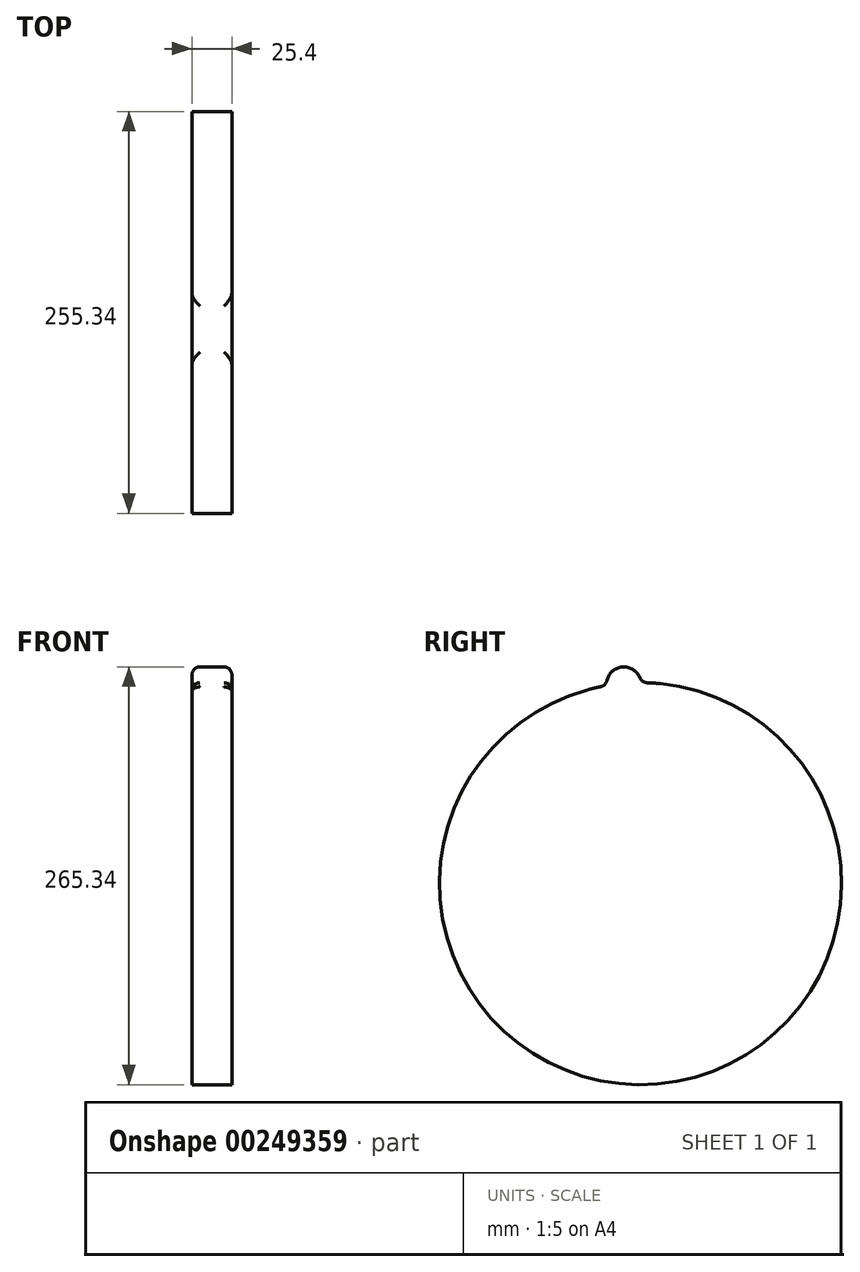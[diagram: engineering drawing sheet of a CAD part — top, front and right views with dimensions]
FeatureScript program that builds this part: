
annotation { "Feature Type Name" : "Feature", "Feature Type Description" : "" }
export const myFeature = defineFeature(function(context is Context, id is Id, definition is map)
    precondition{}
    {
        {
            var Q0;
            Q0=qCreatedBy(makeId("Right.planeOp"),FACE);
            var sketch = newSketch(context, id + "F0", { "sketchPlane" : qUnion([Q0])});
            skCircle(sketch, "E0", {"center": v(0, 0) * mm, "radius": 127.67 * mm});
            skSolve(sketch);
        }
        {
            var Q0;
            Q0=makeQuery(id+"F0.imprint","IMPRINT",FACE,{"disambiguationData":[TD([[makeQuery(id+"F0.imprint","IMPRINT",EDGE,{"derivedFrom":sQuery(id+"F0.wireOp",EDGE,"E0")}),1.0]])]});
            var sketch = newSketch(context, id + "F1", { "sketchPlane" : qUnion([Q0])});
            skCircle(sketch, "E1", {"center": v(-10.62, 126.68) * mm, "radius": 11 * mm});
            skSolve(sketch);
        }
        {
            var Q0;
            Q0=makeQuery(id+"FbJOAYsaVXvaVcf_0.36.F1.imprint","IMPRINT",FACE,{"disambiguationData":[TD([[makeQuery(id+"FbJOAYsaVXvaVcf_0.36.F1.imprint","IMPRINT",EDGE,{"derivedFrom":sQuery(id+"FbJOAYsaVXvaVcf_0.36.F1.wireOp",EDGE,"E1")}),1.0]])]});
            var Q1;
            Q1=makeQuery(id+"FbJOAYsaVXvaVcf_0.32.F1.imprint","IMPRINT",FACE,{"disambiguationData":[TD([[makeQuery(id+"FbJOAYsaVXvaVcf_0.32.F1.imprint","IMPRINT",EDGE,{"derivedFrom":sQuery(id+"FbJOAYsaVXvaVcf_0.32.F1.wireOp",EDGE,"E1")}),1.0]])]});
            var Q2;
            Q2=makeQuery(id+"FbJOAYsaVXvaVcf_0.42.F1.imprint","IMPRINT",FACE,{"disambiguationData":[TD([[makeQuery(id+"FbJOAYsaVXvaVcf_0.42.F1.imprint","IMPRINT",EDGE,{"derivedFrom":sQuery(id+"FbJOAYsaVXvaVcf_0.42.F1.wireOp",EDGE,"E1")}),1.0]])]});
            var Q3;
            Q3=makeQuery(id+"FbJOAYsaVXvaVcf_0.37.F1.imprint","IMPRINT",FACE,{"disambiguationData":[TD([[makeQuery(id+"FbJOAYsaVXvaVcf_0.37.F1.imprint","IMPRINT",EDGE,{"derivedFrom":sQuery(id+"FbJOAYsaVXvaVcf_0.37.F1.wireOp",EDGE,"E1")}),1.0]])]});
            var Q4;
            {var subQ0=sQuery(id+"F1.wireOp",EDGE,"E1");var subQ1=makeQuery(id+"F0.imprint","IMPRINT",EDGE,{"derivedFrom":sQuery(id+"F0.wireOp",EDGE,"E0")});var subQ2=makeQuery(id+"F1.imprint","INTERSECT",VERTEX,{"disambiguationData":[OD(0.0)],"derivedFrom":[subQ1,subQ0]});Q4=makeQuery(id+"F1.imprint","IMPRINT",FACE,{"disambiguationData":[TD([[makeQuery(id+"F1.imprint","IMPRINT",EDGE,{"disambiguationData":[TD([[subQ2,-1.0]])],"derivedFrom":subQ0}),1.0]])]});}
            var Q5;
            Q5=makeQuery(id+"FbJOAYsaVXvaVcf_0.4.F1.imprint","IMPRINT",FACE,{"disambiguationData":[TD([[makeQuery(id+"FbJOAYsaVXvaVcf_0.4.F1.imprint","IMPRINT",EDGE,{"derivedFrom":sQuery(id+"FbJOAYsaVXvaVcf_0.4.F1.wireOp",EDGE,"E1")}),1.0]])]});
            var Q6;
            Q6=makeQuery(id+"FbJOAYsaVXvaVcf_0.22.F1.imprint","IMPRINT",FACE,{"disambiguationData":[TD([[makeQuery(id+"FbJOAYsaVXvaVcf_0.22.F1.imprint","IMPRINT",EDGE,{"derivedFrom":sQuery(id+"FbJOAYsaVXvaVcf_0.22.F1.wireOp",EDGE,"E1")}),1.0]])]});
            var Q7;
            Q7=makeQuery(id+"FbJOAYsaVXvaVcf_0.9.F1.imprint","IMPRINT",FACE,{"disambiguationData":[TD([[makeQuery(id+"FbJOAYsaVXvaVcf_0.9.F1.imprint","IMPRINT",EDGE,{"derivedFrom":sQuery(id+"FbJOAYsaVXvaVcf_0.9.F1.wireOp",EDGE,"E1")}),1.0]])]});
            var Q8;
            Q8=makeQuery(id+"FbJOAYsaVXvaVcf_0.38.F1.imprint","IMPRINT",FACE,{"disambiguationData":[TD([[makeQuery(id+"FbJOAYsaVXvaVcf_0.38.F1.imprint","IMPRINT",EDGE,{"derivedFrom":sQuery(id+"FbJOAYsaVXvaVcf_0.38.F1.wireOp",EDGE,"E1")}),1.0]])]});
            var Q9;
            Q9=makeQuery(id+"FbJOAYsaVXvaVcf_0.3.F1.imprint","IMPRINT",FACE,{"disambiguationData":[TD([[makeQuery(id+"FbJOAYsaVXvaVcf_0.3.F1.imprint","IMPRINT",EDGE,{"derivedFrom":sQuery(id+"FbJOAYsaVXvaVcf_0.3.F1.wireOp",EDGE,"E1")}),1.0]])]});
            var Q10;
            Q10=makeQuery(id+"FbJOAYsaVXvaVcf_0.34.F1.imprint","IMPRINT",FACE,{"disambiguationData":[TD([[makeQuery(id+"FbJOAYsaVXvaVcf_0.34.F1.imprint","IMPRINT",EDGE,{"derivedFrom":sQuery(id+"FbJOAYsaVXvaVcf_0.34.F1.wireOp",EDGE,"E1")}),1.0]])]});
            var Q11;
            Q11=makeQuery(id+"FbJOAYsaVXvaVcf_0.30.F1.imprint","IMPRINT",FACE,{"disambiguationData":[TD([[makeQuery(id+"FbJOAYsaVXvaVcf_0.30.F1.imprint","IMPRINT",EDGE,{"derivedFrom":sQuery(id+"FbJOAYsaVXvaVcf_0.30.F1.wireOp",EDGE,"E1")}),1.0]])]});
            var Q12;
            Q12=makeQuery(id+"FbJOAYsaVXvaVcf_0.48.F1.imprint","IMPRINT",FACE,{"disambiguationData":[TD([[makeQuery(id+"FbJOAYsaVXvaVcf_0.48.F1.imprint","IMPRINT",EDGE,{"derivedFrom":sQuery(id+"FbJOAYsaVXvaVcf_0.48.F1.wireOp",EDGE,"E1")}),1.0]])]});
            var Q13;
            Q13=makeQuery(id+"FbJOAYsaVXvaVcf_0.44.F1.imprint","IMPRINT",FACE,{"disambiguationData":[TD([[makeQuery(id+"FbJOAYsaVXvaVcf_0.44.F1.imprint","IMPRINT",EDGE,{"derivedFrom":sQuery(id+"FbJOAYsaVXvaVcf_0.44.F1.wireOp",EDGE,"E1")}),1.0]])]});
            var Q14;
            Q14=makeQuery(id+"FbJOAYsaVXvaVcf_0.2.F1.imprint","IMPRINT",FACE,{"disambiguationData":[TD([[makeQuery(id+"FbJOAYsaVXvaVcf_0.2.F1.imprint","IMPRINT",EDGE,{"derivedFrom":sQuery(id+"FbJOAYsaVXvaVcf_0.2.F1.wireOp",EDGE,"E1")}),1.0]])]});
            var Q15;
            Q15=makeQuery(id+"FbJOAYsaVXvaVcf_0.39.F1.imprint","IMPRINT",FACE,{"disambiguationData":[TD([[makeQuery(id+"FbJOAYsaVXvaVcf_0.39.F1.imprint","IMPRINT",EDGE,{"derivedFrom":sQuery(id+"FbJOAYsaVXvaVcf_0.39.F1.wireOp",EDGE,"E1")}),1.0]])]});
            var Q16;
            Q16=makeQuery(id+"FbJOAYsaVXvaVcf_0.27.F1.imprint","IMPRINT",FACE,{"disambiguationData":[TD([[makeQuery(id+"FbJOAYsaVXvaVcf_0.27.F1.imprint","IMPRINT",EDGE,{"derivedFrom":sQuery(id+"FbJOAYsaVXvaVcf_0.27.F1.wireOp",EDGE,"E1")}),1.0]])]});
            var Q17;
            Q17=makeQuery(id+"FbJOAYsaVXvaVcf_0.1.F1.imprint","IMPRINT",FACE,{"disambiguationData":[TD([[makeQuery(id+"FbJOAYsaVXvaVcf_0.1.F1.imprint","IMPRINT",EDGE,{"derivedFrom":sQuery(id+"FbJOAYsaVXvaVcf_0.1.F1.wireOp",EDGE,"E1")}),1.0]])]});
            var Q18;
            Q18=makeQuery(id+"FbJOAYsaVXvaVcf_0.35.F1.imprint","IMPRINT",FACE,{"disambiguationData":[TD([[makeQuery(id+"FbJOAYsaVXvaVcf_0.35.F1.imprint","IMPRINT",EDGE,{"derivedFrom":sQuery(id+"FbJOAYsaVXvaVcf_0.35.F1.wireOp",EDGE,"E1")}),1.0]])]});
            var Q19;
            Q19=makeQuery(id+"FbJOAYsaVXvaVcf_0.31.F1.imprint","IMPRINT",FACE,{"disambiguationData":[TD([[makeQuery(id+"FbJOAYsaVXvaVcf_0.31.F1.imprint","IMPRINT",EDGE,{"derivedFrom":sQuery(id+"FbJOAYsaVXvaVcf_0.31.F1.wireOp",EDGE,"E1")}),1.0]])]});
            var Q20;
            Q20=makeQuery(id+"FbJOAYsaVXvaVcf_0.45.F1.imprint","IMPRINT",FACE,{"disambiguationData":[TD([[makeQuery(id+"FbJOAYsaVXvaVcf_0.45.F1.imprint","IMPRINT",EDGE,{"derivedFrom":sQuery(id+"FbJOAYsaVXvaVcf_0.45.F1.wireOp",EDGE,"E1")}),1.0]])]});
            var Q21;
            Q21=makeQuery(id+"FbJOAYsaVXvaVcf_0.41.F1.imprint","IMPRINT",FACE,{"disambiguationData":[TD([[makeQuery(id+"FbJOAYsaVXvaVcf_0.41.F1.imprint","IMPRINT",EDGE,{"derivedFrom":sQuery(id+"FbJOAYsaVXvaVcf_0.41.F1.wireOp",EDGE,"E1")}),1.0]])]});
            var Q22;
            Q22=makeQuery(id+"FbJOAYsaVXvaVcf_0.40.F1.imprint","IMPRINT",FACE,{"disambiguationData":[TD([[makeQuery(id+"FbJOAYsaVXvaVcf_0.40.F1.imprint","IMPRINT",EDGE,{"derivedFrom":sQuery(id+"FbJOAYsaVXvaVcf_0.40.F1.wireOp",EDGE,"E1")}),1.0]])]});
            var Q23;
            {var subQ0=sQuery(id+"F1.wireOp",EDGE,"E1");var subQ1=makeQuery(id+"F0.imprint","IMPRINT",EDGE,{"derivedFrom":sQuery(id+"F0.wireOp",EDGE,"E0")});var subQ2=makeQuery(id+"F1.imprint","INTERSECT",VERTEX,{"disambiguationData":[OD(0.0)],"derivedFrom":[subQ1,subQ0]});Q23=makeQuery(id+"F1.imprint","IMPRINT",FACE,{"disambiguationData":[TD([[makeQuery(id+"F1.imprint","IMPRINT",EDGE,{"disambiguationData":[TD([[subQ2,1.0]])],"derivedFrom":subQ0}),1.0]])]});}
            var Q24;
            Q24=makeQuery(id+"FbJOAYsaVXvaVcf_0.8.F1.imprint","IMPRINT",FACE,{"disambiguationData":[TD([[makeQuery(id+"FbJOAYsaVXvaVcf_0.8.F1.imprint","IMPRINT",EDGE,{"derivedFrom":sQuery(id+"FbJOAYsaVXvaVcf_0.8.F1.wireOp",EDGE,"E1")}),1.0]])]});
            var Q25;
            Q25=makeQuery(id+"FbJOAYsaVXvaVcf_0.26.F1.imprint","IMPRINT",FACE,{"disambiguationData":[TD([[makeQuery(id+"FbJOAYsaVXvaVcf_0.26.F1.imprint","IMPRINT",EDGE,{"derivedFrom":sQuery(id+"FbJOAYsaVXvaVcf_0.26.F1.wireOp",EDGE,"E1")}),1.0]])]});
            var Q26;
            Q26=makeQuery(id+"FbJOAYsaVXvaVcf_0.49.F1.imprint","IMPRINT",FACE,{"disambiguationData":[TD([[makeQuery(id+"FbJOAYsaVXvaVcf_0.49.F1.imprint","IMPRINT",EDGE,{"derivedFrom":sQuery(id+"FbJOAYsaVXvaVcf_0.49.F1.wireOp",EDGE,"E1")}),1.0]])]});
            var Q27;
            Q27=makeQuery(id+"FbJOAYsaVXvaVcf_0.21.F1.imprint","IMPRINT",FACE,{"disambiguationData":[TD([[makeQuery(id+"FbJOAYsaVXvaVcf_0.21.F1.imprint","IMPRINT",EDGE,{"derivedFrom":sQuery(id+"FbJOAYsaVXvaVcf_0.21.F1.wireOp",EDGE,"E1")}),1.0]])]});
            var Q28;
            Q28=makeQuery(id+"FbJOAYsaVXvaVcf_0.7.F1.imprint","IMPRINT",FACE,{"disambiguationData":[TD([[makeQuery(id+"FbJOAYsaVXvaVcf_0.7.F1.imprint","IMPRINT",EDGE,{"derivedFrom":sQuery(id+"FbJOAYsaVXvaVcf_0.7.F1.wireOp",EDGE,"E1")}),1.0]])]});
            var Q29;
            Q29=makeQuery(id+"FbJOAYsaVXvaVcf_0.28.F1.imprint","IMPRINT",FACE,{"disambiguationData":[TD([[makeQuery(id+"FbJOAYsaVXvaVcf_0.28.F1.imprint","IMPRINT",EDGE,{"derivedFrom":sQuery(id+"FbJOAYsaVXvaVcf_0.28.F1.wireOp",EDGE,"E1")}),1.0]])]});
            var Q30;
            Q30=makeQuery(id+"FbJOAYsaVXvaVcf_0.25.F1.imprint","IMPRINT",FACE,{"disambiguationData":[TD([[makeQuery(id+"FbJOAYsaVXvaVcf_0.25.F1.imprint","IMPRINT",EDGE,{"derivedFrom":sQuery(id+"FbJOAYsaVXvaVcf_0.25.F1.wireOp",EDGE,"E1")}),1.0]])]});
            var Q31;
            Q31=makeQuery(id+"FbJOAYsaVXvaVcf_0.46.F1.imprint","IMPRINT",FACE,{"disambiguationData":[TD([[makeQuery(id+"FbJOAYsaVXvaVcf_0.46.F1.imprint","IMPRINT",EDGE,{"derivedFrom":sQuery(id+"FbJOAYsaVXvaVcf_0.46.F1.wireOp",EDGE,"E1")}),1.0]])]});
            var Q32;
            Q32=makeQuery(id+"FbJOAYsaVXvaVcf_0.20.F1.imprint","IMPRINT",FACE,{"disambiguationData":[TD([[makeQuery(id+"FbJOAYsaVXvaVcf_0.20.F1.imprint","IMPRINT",EDGE,{"derivedFrom":sQuery(id+"FbJOAYsaVXvaVcf_0.20.F1.wireOp",EDGE,"E1")}),1.0]])]});
            var Q33;
            Q33=makeQuery(id+"FbJOAYsaVXvaVcf_0.6.F1.imprint","IMPRINT",FACE,{"disambiguationData":[TD([[makeQuery(id+"FbJOAYsaVXvaVcf_0.6.F1.imprint","IMPRINT",EDGE,{"derivedFrom":sQuery(id+"FbJOAYsaVXvaVcf_0.6.F1.wireOp",EDGE,"E1")}),1.0]])]});
            var Q34;
            Q34=makeQuery(id+"FbJOAYsaVXvaVcf_0.24.F1.imprint","IMPRINT",FACE,{"disambiguationData":[TD([[makeQuery(id+"FbJOAYsaVXvaVcf_0.24.F1.imprint","IMPRINT",EDGE,{"derivedFrom":sQuery(id+"FbJOAYsaVXvaVcf_0.24.F1.wireOp",EDGE,"E1")}),1.0]])]});
            var Q35;
            Q35=makeQuery(id+"FbJOAYsaVXvaVcf_0.19.F1.imprint","IMPRINT",FACE,{"disambiguationData":[TD([[makeQuery(id+"FbJOAYsaVXvaVcf_0.19.F1.imprint","IMPRINT",EDGE,{"derivedFrom":sQuery(id+"FbJOAYsaVXvaVcf_0.19.F1.wireOp",EDGE,"E1")}),1.0]])]});
            var Q36;
            Q36=makeQuery(id+"FbJOAYsaVXvaVcf_0.33.F1.imprint","IMPRINT",FACE,{"disambiguationData":[TD([[makeQuery(id+"FbJOAYsaVXvaVcf_0.33.F1.imprint","IMPRINT",EDGE,{"derivedFrom":sQuery(id+"FbJOAYsaVXvaVcf_0.33.F1.wireOp",EDGE,"E1")}),1.0]])]});
            var Q37;
            Q37=makeQuery(id+"FbJOAYsaVXvaVcf_0.5.F1.imprint","IMPRINT",FACE,{"disambiguationData":[TD([[makeQuery(id+"FbJOAYsaVXvaVcf_0.5.F1.imprint","IMPRINT",EDGE,{"derivedFrom":sQuery(id+"FbJOAYsaVXvaVcf_0.5.F1.wireOp",EDGE,"E1")}),1.0]])]});
            var Q38;
            Q38=makeQuery(id+"FbJOAYsaVXvaVcf_0.23.F1.imprint","IMPRINT",FACE,{"disambiguationData":[TD([[makeQuery(id+"FbJOAYsaVXvaVcf_0.23.F1.imprint","IMPRINT",EDGE,{"derivedFrom":sQuery(id+"FbJOAYsaVXvaVcf_0.23.F1.wireOp",EDGE,"E1")}),1.0]])]});
            var Q39;
            Q39=makeQuery(id+"FbJOAYsaVXvaVcf_0.29.F1.imprint","IMPRINT",FACE,{"disambiguationData":[TD([[makeQuery(id+"FbJOAYsaVXvaVcf_0.29.F1.imprint","IMPRINT",EDGE,{"derivedFrom":sQuery(id+"FbJOAYsaVXvaVcf_0.29.F1.wireOp",EDGE,"E1")}),1.0]])]});
            var Q40;
            Q40=makeQuery(id+"FbJOAYsaVXvaVcf_0.43.F1.imprint","IMPRINT",FACE,{"disambiguationData":[TD([[makeQuery(id+"FbJOAYsaVXvaVcf_0.43.F1.imprint","IMPRINT",EDGE,{"derivedFrom":sQuery(id+"FbJOAYsaVXvaVcf_0.43.F1.wireOp",EDGE,"E1")}),1.0]])]});
            var Q41;
            Q41=makeQuery(id+"FbJOAYsaVXvaVcf_0.47.F1.imprint","IMPRINT",FACE,{"disambiguationData":[TD([[makeQuery(id+"FbJOAYsaVXvaVcf_0.47.F1.imprint","IMPRINT",EDGE,{"derivedFrom":sQuery(id+"FbJOAYsaVXvaVcf_0.47.F1.wireOp",EDGE,"E1")}),1.0]])]});
            var Q42;
            Q42=makeQuery(id+"FbJOAYsaVXvaVcf_0.17.F1.imprint","IMPRINT",FACE,{"disambiguationData":[TD([[makeQuery(id+"FbJOAYsaVXvaVcf_0.17.F1.imprint","IMPRINT",EDGE,{"derivedFrom":sQuery(id+"FbJOAYsaVXvaVcf_0.17.F1.wireOp",EDGE,"E1")}),1.0]])]});
            var Q43;
            Q43=makeQuery(id+"FbJOAYsaVXvaVcf_0.12.F1.imprint","IMPRINT",FACE,{"disambiguationData":[TD([[makeQuery(id+"FbJOAYsaVXvaVcf_0.12.F1.imprint","IMPRINT",EDGE,{"derivedFrom":sQuery(id+"FbJOAYsaVXvaVcf_0.12.F1.wireOp",EDGE,"E1")}),1.0]])]});
            var Q44;
            Q44=makeQuery(id+"FbJOAYsaVXvaVcf_0.11.F1.imprint","IMPRINT",FACE,{"disambiguationData":[TD([[makeQuery(id+"FbJOAYsaVXvaVcf_0.11.F1.imprint","IMPRINT",EDGE,{"derivedFrom":sQuery(id+"FbJOAYsaVXvaVcf_0.11.F1.wireOp",EDGE,"E1")}),1.0]])]});
            var Q45;
            Q45=makeQuery(id+"FbJOAYsaVXvaVcf_0.15.F1.imprint","IMPRINT",FACE,{"disambiguationData":[TD([[makeQuery(id+"FbJOAYsaVXvaVcf_0.15.F1.imprint","IMPRINT",EDGE,{"derivedFrom":sQuery(id+"FbJOAYsaVXvaVcf_0.15.F1.wireOp",EDGE,"E1")}),1.0]])]});
            var Q46;
            Q46=makeQuery(id+"FbJOAYsaVXvaVcf_0.16.F1.imprint","IMPRINT",FACE,{"disambiguationData":[TD([[makeQuery(id+"FbJOAYsaVXvaVcf_0.16.F1.imprint","IMPRINT",EDGE,{"derivedFrom":sQuery(id+"FbJOAYsaVXvaVcf_0.16.F1.wireOp",EDGE,"E1")}),1.0]])]});
            var Q47;
            Q47=makeQuery(id+"FbJOAYsaVXvaVcf_0.14.F1.imprint","IMPRINT",FACE,{"disambiguationData":[TD([[makeQuery(id+"FbJOAYsaVXvaVcf_0.14.F1.imprint","IMPRINT",EDGE,{"derivedFrom":sQuery(id+"FbJOAYsaVXvaVcf_0.14.F1.wireOp",EDGE,"E1")}),1.0]])]});
            var Q48;
            Q48=makeQuery(id+"FbJOAYsaVXvaVcf_0.13.F1.imprint","IMPRINT",FACE,{"disambiguationData":[TD([[makeQuery(id+"FbJOAYsaVXvaVcf_0.13.F1.imprint","IMPRINT",EDGE,{"derivedFrom":sQuery(id+"FbJOAYsaVXvaVcf_0.13.F1.wireOp",EDGE,"E1")}),1.0]])]});
            var Q49;
            Q49=makeQuery(id+"FbJOAYsaVXvaVcf_0.10.F1.imprint","IMPRINT",FACE,{"disambiguationData":[TD([[makeQuery(id+"FbJOAYsaVXvaVcf_0.10.F1.imprint","IMPRINT",EDGE,{"derivedFrom":sQuery(id+"FbJOAYsaVXvaVcf_0.10.F1.wireOp",EDGE,"E1")}),1.0]])]});
            var Q50;
            Q50=makeQuery(id+"FbJOAYsaVXvaVcf_0.18.F1.imprint","IMPRINT",FACE,{"disambiguationData":[TD([[makeQuery(id+"FbJOAYsaVXvaVcf_0.18.F1.imprint","IMPRINT",EDGE,{"derivedFrom":sQuery(id+"FbJOAYsaVXvaVcf_0.18.F1.wireOp",EDGE,"E1")}),1.0]])]});
            var Q51;
            {var subQ0=sQuery(id+"F1.wireOp",EDGE,"E1");var subQ1=makeQuery(id+"F0.imprint","IMPRINT",EDGE,{"derivedFrom":sQuery(id+"F0.wireOp",EDGE,"E0")});var subQ2=makeQuery(id+"F1.imprint","INTERSECT",VERTEX,{"disambiguationData":[OD(0.0)],"derivedFrom":[subQ1,subQ0]});Q51=makeQuery(id+"F1.imprint","IMPRINT",FACE,{"disambiguationData":[TD([[makeQuery(id+"F1.imprint","IMPRINT",EDGE,{"disambiguationData":[TD([[subQ2,-1.0]])],"derivedFrom":subQ0}),-1.0]])]});}
            extrude(context, id + "F2", {"entities" : qUnion([Q0, Q1, Q2, Q3, Q4, Q5, Q6, Q7, Q8, Q9, Q10, Q11, Q12, Q13, Q14, Q15, Q16, Q17, Q18, Q19, Q20, Q21, Q22, Q23, Q24, Q25, Q26, Q27, Q28, Q29, Q30, Q31, Q32, Q33, Q34, Q35, Q36, Q37, Q38, Q39, Q40, Q41, Q42, Q43, Q44, Q45, Q46, Q47, Q48, Q49, Q50, Q51]), "depth" : 25.4 * mm});
        }
        {
            var Q0;
            Q0=makeQuery(id+"F2.opExtrude","SWEPT_FACE",FACE,{"disambiguationData":[OSD([sQuery(id+"F1.wireOp",EDGE,"E1")])]});
            var Q1;
            Q1=makeQuery(id+"F2.opExtrude","SWEPT_FACE",FACE,{"disambiguationData":[OSD([sQuery(id+"FbJOAYsaVXvaVcf_0.1.F1.wireOp",EDGE,"E1")])]});
            fillet(context, id + "F3", {"entities" : qUnion([Q0, Q1]), "radius" : 5.08 * mm, "tangentPropagation" : true, "allowEdgeOverflow" : false});
        }
    });
